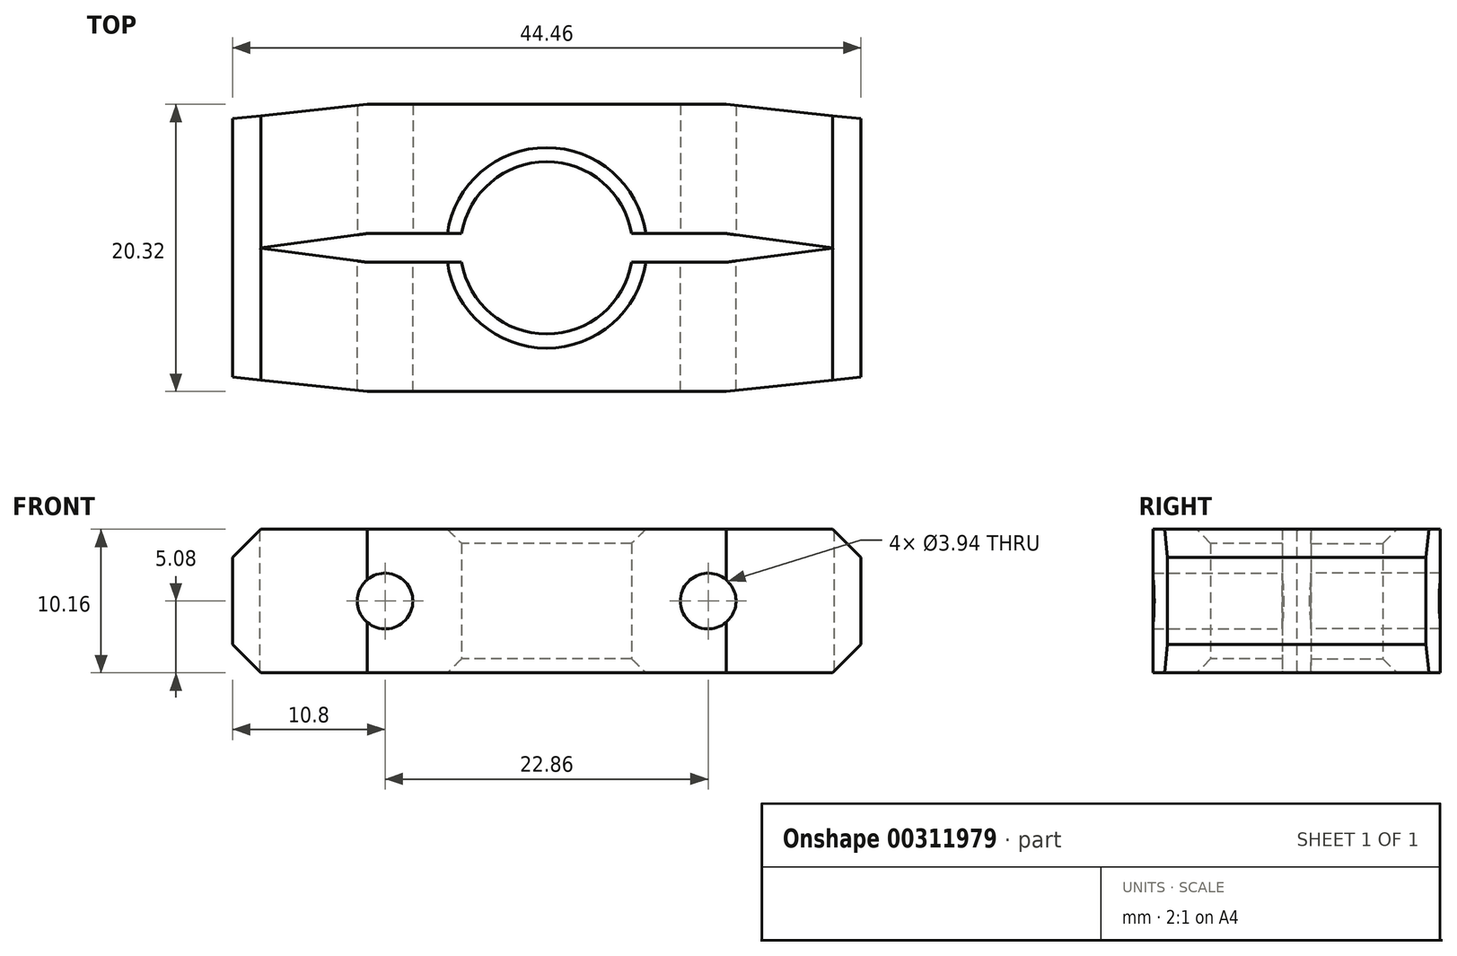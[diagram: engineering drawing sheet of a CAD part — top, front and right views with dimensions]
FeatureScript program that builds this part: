
annotation { "Feature Type Name" : "Feature", "Feature Type Description" : "" }
export const myFeature = defineFeature(function(context is Context, id is Id, definition is map)
    precondition{}
    {
        {
            var Q0;
            Q0=qCreatedBy(makeId("Top.planeOp"),FACE);
            var sketch = newSketch(context, id + "F0", { "sketchPlane" : qUnion([Q0])});
            skLineSegment(sketch, "E0.bottom", {"start": v(12.7, -10.16) * mm, "end": v(-12.7, -10.16) * mm});
            skLineSegment(sketch, "E0.top", {"start": v(12.7, 10.16) * mm, "end": v(-12.7, 10.16) * mm});
            skLineSegment(sketch, "E0.left", {"start": v(22.23, -9.14) * mm, "end": v(22.22, 9.14) * mm});
            skLineSegment(sketch, "E0.right", {"start": v(-22.23, -9.14) * mm, "end": v(-22.23, 9.14) * mm});
            skPoint(sketch, "E0.middle", {"position": v(0, 0) * mm});
            skArc(sketch, "E1", {"start": v(-6.01, -1.02) * mm, "mid": v(0, -6.1) * mm, "end": v(6.01, -1.02) * mm});
            skArc(sketch, "E2.trimOffspring", {"start": v(6.01, 1.02) * mm, "mid": v(0, 6.1) * mm, "end": v(-6.01, 1.02) * mm});
            skLineSegment(sketch, "E3", {"start": v(-6.01, 1.02) * mm, "end": v(-12.7, 1.02) * mm});
            skLineSegment(sketch, "E4", {"start": v(-6.01, -1.02) * mm, "end": v(-12.7, -1.02) * mm});
            skLineSegment(sketch, "E5", {"start": v(-12.7, -1.02) * mm, "end": v(-20.32, 0) * mm});
            skLineSegment(sketch, "E6", {"start": v(-20.32, 0) * mm, "end": v(-12.7, 1.02) * mm});
            skLineSegment(sketch, "E7.MirrorCS", {"start": v(6.01, 1.02) * mm, "end": v(12.7, 1.02) * mm});
            skLineSegment(sketch, "E8.MirrorCS", {"start": v(20.32, 0) * mm, "end": v(12.7, 1.02) * mm});
            skLineSegment(sketch, "E9.MirrorCS", {"start": v(12.7, -1.02) * mm, "end": v(20.32, 0) * mm});
            skLineSegment(sketch, "E10.MirrorCS", {"start": v(6.01, -1.02) * mm, "end": v(12.7, -1.02) * mm});
            skLineSegment(sketch, "E11", {"start": v(-22.23, 9.14) * mm, "end": v(-12.7, 10.16) * mm});
            skLineSegment(sketch, "E12.MirrorCS", {"start": v(-22.23, -9.14) * mm, "end": v(-12.7, -10.16) * mm});
            skLineSegment(sketch, "E13.MirrorCS", {"start": v(22.23, 9.14) * mm, "end": v(12.7, 10.16) * mm});
            skLineSegment(sketch, "E14.MirrorCS", {"start": v(22.23, -9.14) * mm, "end": v(12.7, -10.16) * mm});
            skSolve(sketch);
        }
        {
            var Q0;
            Q0 = qSketchRegion(id + "F0", true);
            extrude(context, id + "F1", {"entities" : qUnion([Q0]), "endBound" : BoundingType.SYMMETRIC, "depth" : 10.16 * mm});
        }
        {
            var Q0;
            Q0=qCreatedBy(makeId("Front.planeOp"),FACE);
            var sketch = newSketch(context, id + "F2", { "sketchPlane" : qUnion([Q0])});
            skPoint(sketch, "E15", {"position": v(-11.43, 0) * mm});
            skPoint(sketch, "E16", {"position": v(11.43, 0) * mm});
            skSolve(sketch);
        }
        {
            var Q0;
            Q0=sQuery(id+"F2.wireOp",VERTEX,"E15");
            var Q1;
            Q1=sQuery(id+"F2.wireOp",VERTEX,"E16");
            var Q2;
            Q2=makeQuery(id+"F1.opExtrude","SWEPT_BODY",BODY,{"disambiguationData":[OSD([sQuery(id+"F0.wireOp",EDGE,"E0.bottom"),sQuery(id+"F0.wireOp",EDGE,"E0.top"),sQuery(id+"F0.wireOp",EDGE,"E0.left"),sQuery(id+"F0.wireOp",EDGE,"E0.right"),sQuery(id+"F0.wireOp",EDGE,"E1"),sQuery(id+"F0.wireOp",EDGE,"n1T6Ejxo-1DgY-EBuP-pgv1-Msir6xzyjba1.bottom"),sQuery(id+"F0.wireOp",EDGE,"n1T6Ejxo-1DgY-EBuP-pgv1-Msir6xzyjba1.top"),sQuery(id+"F0.wireOp",EDGE,"n1T6Ejxo-1DgY-EBuP-pgv1-Msir6xzyjba1.right"),sQuery(id+"F0.wireOp",EDGE,"1520d7f2-2a1a-453c-9e2a-3872f5004d490.MirrorCS"),sQuery(id+"F0.wireOp",EDGE,"1520d7f2-2a1a-453c-9e2a-3872f5004d491.MirrorCS"),sQuery(id+"F0.wireOp",EDGE,"1520d7f2-2a1a-453c-9e2a-3872f5004d492.MirrorCS"),sQuery(id+"F0.wireOp",EDGE,"E2.trimOffspring")])]});
            hole(context, id + "F3", {"style" : HoleStyle.SIMPLE, "endStyle" : HoleEndStyle.BLIND, "holeDiameter" : 3.94 * mm, "holeDepth" : 12.7 * mm, "tappedDepth" : 12.7 * mm, "tapClearance" : 3, "locations" : qUnion([Q0, Q1]), "scope" : qUnion([Q2])});
        }
        {
            var Q0;
            Q0=sQuery(id+"F2.wireOp",VERTEX,"E15");
            var Q1;
            Q1=sQuery(id+"F2.wireOp",VERTEX,"E16");
            var Q2;
            Q2=makeQuery(id+"F1.opExtrude","SWEPT_BODY",BODY,{"disambiguationData":[OSD([sQuery(id+"F0.wireOp",EDGE,"E0.bottom"),sQuery(id+"F0.wireOp",EDGE,"E0.top"),sQuery(id+"F0.wireOp",EDGE,"E0.left"),sQuery(id+"F0.wireOp",EDGE,"E0.right"),sQuery(id+"F0.wireOp",EDGE,"E1"),sQuery(id+"F0.wireOp",EDGE,"n1T6Ejxo-1DgY-EBuP-pgv1-Msir6xzyjba1.bottom"),sQuery(id+"F0.wireOp",EDGE,"n1T6Ejxo-1DgY-EBuP-pgv1-Msir6xzyjba1.top"),sQuery(id+"F0.wireOp",EDGE,"n1T6Ejxo-1DgY-EBuP-pgv1-Msir6xzyjba1.right"),sQuery(id+"F0.wireOp",EDGE,"1520d7f2-2a1a-453c-9e2a-3872f5004d490.MirrorCS"),sQuery(id+"F0.wireOp",EDGE,"1520d7f2-2a1a-453c-9e2a-3872f5004d491.MirrorCS"),sQuery(id+"F0.wireOp",EDGE,"1520d7f2-2a1a-453c-9e2a-3872f5004d492.MirrorCS"),sQuery(id+"F0.wireOp",EDGE,"E2.trimOffspring")])]});
            hole(context, id + "F4", {"style" : HoleStyle.SIMPLE, "endStyle" : HoleEndStyle.BLIND, "oppositeDirection" : true, "holeDiameter" : 3.94 * mm, "holeDepth" : 12.7 * mm, "tappedDepth" : 12.7 * mm, "tapClearance" : 3, "locations" : qUnion([Q0, Q1]), "scope" : qUnion([Q2])});
        }
        {
            var Q0;
            Q0=makeQuery(id+"F1.opExtrude","CAP_EDGE",EDGE,{"disambiguationData":[OSD([sQuery(id+"F0.wireOp",EDGE,"E0.left")])],"isStart":true});
            var Q1;
            Q1=makeQuery(id+"F1.opExtrude","CAP_EDGE",EDGE,{"disambiguationData":[OSD([sQuery(id+"F0.wireOp",EDGE,"E0.left")])],"isStart":false});
            var Q2;
            Q2=makeQuery(id+"F1.opExtrude","CAP_EDGE",EDGE,{"disambiguationData":[OSD([sQuery(id+"F0.wireOp",EDGE,"E0.right")])],"isStart":false});
            var Q3;
            Q3=makeQuery(id+"F1.opExtrude","CAP_EDGE",EDGE,{"disambiguationData":[OSD([sQuery(id+"F0.wireOp",EDGE,"E0.right")])],"isStart":true});
            chamfer(context, id + "F5", {"entities" : qUnion([Q0, Q1, Q2, Q3]), "width" : 2 * mm, "tangentPropagation" : true});
        }
        {
            var Q0;
            Q0=makeQuery(id+"F1.opExtrude","CAP_EDGE",EDGE,{"disambiguationData":[OSD([sQuery(id+"F0.wireOp",EDGE,"E1")])],"isStart":true});
            var Q1;
            Q1=makeQuery(id+"F1.opExtrude","CAP_EDGE",EDGE,{"disambiguationData":[OSD([sQuery(id+"F0.wireOp",EDGE,"E1")])],"isStart":false});
            var Q2;
            Q2=makeQuery(id+"F1.opExtrude","CAP_EDGE",EDGE,{"disambiguationData":[OSD([sQuery(id+"F0.wireOp",EDGE,"E2.trimOffspring")])],"isStart":false});
            var Q3;
            Q3=makeQuery(id+"F1.opExtrude","CAP_EDGE",EDGE,{"disambiguationData":[OSD([sQuery(id+"F0.wireOp",EDGE,"E2.trimOffspring")])],"isStart":true});
            chamfer(context, id + "F6", {"entities" : qUnion([Q0, Q1, Q2, Q3]), "width" : 1 * mm, "tangentPropagation" : true});
        }
    });
